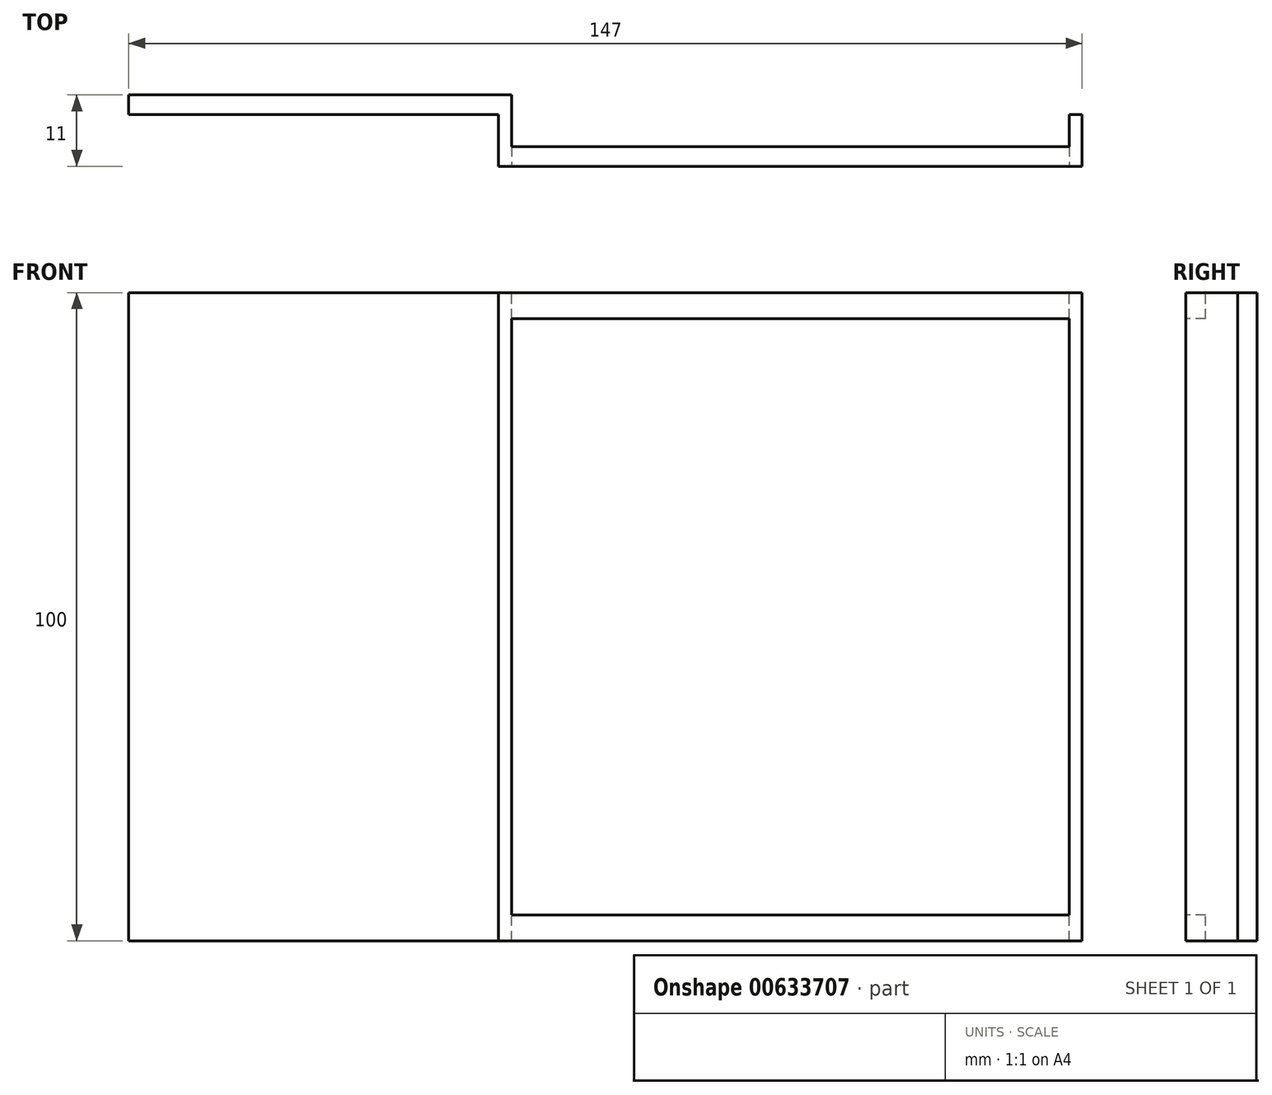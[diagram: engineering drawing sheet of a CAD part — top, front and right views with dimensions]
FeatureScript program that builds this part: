
annotation { "Feature Type Name" : "Feature", "Feature Type Description" : "" }
export const myFeature = defineFeature(function(context is Context, id is Id, definition is map)
    precondition{}
    {
        {
            var Q0;
            Q0=qCreatedBy(makeId("Top.planeOp"),FACE);
            var sketch = newSketch(context, id + "F0", { "sketchPlane" : qUnion([Q0])});
            skLineSegment(sketch, "E0", {"start": v(87.7, 0) * mm, "end": v(-2.3, 0) * mm});
            skLineSegment(sketch, "E1", {"start": v(-2.3, 0) * mm, "end": v(-2.3, 3) * mm});
            skLineSegment(sketch, "E2", {"start": v(-59.3, 11) * mm, "end": v(-0.3, 11) * mm});
            skLineSegment(sketch, "E3", {"start": v(-0.3, 11) * mm, "end": v(-0.3, 3) * mm});
            skLineSegment(sketch, "E4", {"start": v(-0.3, 3) * mm, "end": v(85.7, 3) * mm});
            skLineSegment(sketch, "E5", {"start": v(85.7, 3) * mm, "end": v(85.7, 8) * mm});
            skLineSegment(sketch, "E6", {"start": v(85.7, 8) * mm, "end": v(87.7, 8) * mm});
            skLineSegment(sketch, "E7", {"start": v(87.7, 8) * mm, "end": v(87.7, 0) * mm});
            skLineSegment(sketch, "E8", {"start": v(-59.3, 11) * mm, "end": v(-59.3, 8) * mm});
            skLineSegment(sketch, "E9", {"start": v(-59.3, 8) * mm, "end": v(-2.3, 8) * mm});
            skLineSegment(sketch, "E10", {"start": v(-2.3, 8) * mm, "end": v(-2.3, 3) * mm});
            skSolve(sketch);
        }
        {
            var Q0;
            Q0=makeQuery(id+"F0.imprint","IMPRINT",FACE,{"disambiguationData":[TD([[makeQuery(id+"F0.imprint","IMPRINT",EDGE,{"derivedFrom":sQuery(id+"F0.wireOp",EDGE,"E0")}),-1.0]])]});
            var Q1;
            Q1=sQuery(id+"F0.wireOp",EDGE,"E0");
            var Q2;
            Q2=sQuery(id+"F0.wireOp",EDGE,"E2");
            var Q3;
            Q3=sQuery(id+"F0.wireOp",EDGE,"E9");
            var Q4;
            Q4=sQuery(id+"F0.wireOp",EDGE,"E10");
            var Q5;
            Q5=sQuery(id+"F0.wireOp",EDGE,"E3");
            var Q6;
            Q6=sQuery(id+"F0.wireOp",EDGE,"E7");
            var Q7;
            Q7=sQuery(id+"F0.wireOp",EDGE,"E5");
            var Q8;
            Q8=sQuery(id+"F0.wireOp",EDGE,"E8");
            var Q9;
            Q9=sQuery(id+"F0.wireOp",EDGE,"E6");
            var Q10;
            Q10=sQuery(id+"F0.wireOp",EDGE,"E1");
            var Q11;
            Q11=sQuery(id+"F0.wireOp",EDGE,"E4");
            extrude(context, id + "F1", {"entities" : qUnion([Q0]), "bodyType" : ToolBodyType.SURFACE, "operationType" : NewBodyOperationType.ADD, "surfaceEntities" : qUnion([Q1, Q2, Q3, Q4, Q5, Q6, Q7, Q8, Q9, Q10, Q11]), "oppositeDirection" : true, "depth" : 100 * mm, "offsetDistance" : 25 * mm});
        }
        {
            var Q0;
            Q0 = qSketchRegion(id + "F0", true);
            extrude(context, id + "F2", {"entities" : qUnion([Q0]), "oppositeDirection" : true, "depth" : 100 * mm, "offsetDistance" : 25 * mm});
        }
        {
            var Q0;
            Q0=qCreatedBy(makeId("Front.planeOp"),FACE);
            var sketch = newSketch(context, id + "F3", { "sketchPlane" : qUnion([Q0])});
            skLineSegment(sketch, "E11.bottom", {"start": v(-0.3, -4) * mm, "end": v(85.7, -4) * mm});
            skLineSegment(sketch, "E11.top", {"start": v(-0.3, -96) * mm, "end": v(85.7, -96) * mm});
            skLineSegment(sketch, "E11.left", {"start": v(-0.3, -4) * mm, "end": v(-0.3, -96) * mm});
            skLineSegment(sketch, "E11.right", {"start": v(85.7, -4) * mm, "end": v(85.7, -96) * mm});
            skPoint(sketch, "E12", {"position": v(-56.86, -50.12) * mm});
            skPoint(sketch, "E13", {"position": v(-0.3, -50) * mm});
            skLineSegment(sketch, "E14", {"start": v(-13.3, 0) * mm, "end": v(-13.3, -100) * mm});
            skPoint(sketch, "E15", {"position": v(-13.3, -50) * mm});
            skArc(sketch, "E16", {"start": v(-56.86, -50.12) * mm, "mid": v(-44.15, -19.25) * mm, "end": v(-13.3, -6.44) * mm});
            skArc(sketch, "E17", {"start": v(-13.18, -93.56) * mm, "mid": v(-44.02, -80.89) * mm, "end": v(-56.86, -50.12) * mm});
            skLineSegment(sketch, "E18", {"start": v(-53.6, -33.45) * mm, "end": v(-13.3, -50) * mm});
            skLineSegment(sketch, "E19", {"start": v(-44.2, -19.29) * mm, "end": v(-13.3, -50) * mm});
            skLineSegment(sketch, "E20", {"start": v(-30.09, -9.8) * mm, "end": v(-13.3, -50) * mm});
            skLineSegment(sketch, "E21", {"start": v(-56.86, -50.12) * mm, "end": v(-13.3, -50) * mm});
            skLineSegment(sketch, "E22", {"start": v(-53.5, -66.78) * mm, "end": v(-13.3, -50) * mm});
            skLineSegment(sketch, "E23", {"start": v(-44.02, -80.89) * mm, "end": v(-13.3, -50) * mm});
            skLineSegment(sketch, "E24", {"start": v(-29.86, -90.29) * mm, "end": v(-13.3, -50) * mm});
            skSolve(sketch);
        }
        {
            var Q0;
            Q0=makeQuery(id+"F3.imprint","IMPRINT",FACE,{"disambiguationData":[TD([[makeQuery(id+"F3.imprint","IMPRINT",EDGE,{"derivedFrom":sQuery(id+"F3.wireOp",EDGE,"E11.bottom")}),-1.0]])]});
            extrude(context, id + "F4", {"entities" : qUnion([Q0]), "operationType" : NewBodyOperationType.REMOVE, "oppositeDirection" : true, "depth" : 3 * mm, "offsetDistance" : 25 * mm});
        }
    });
